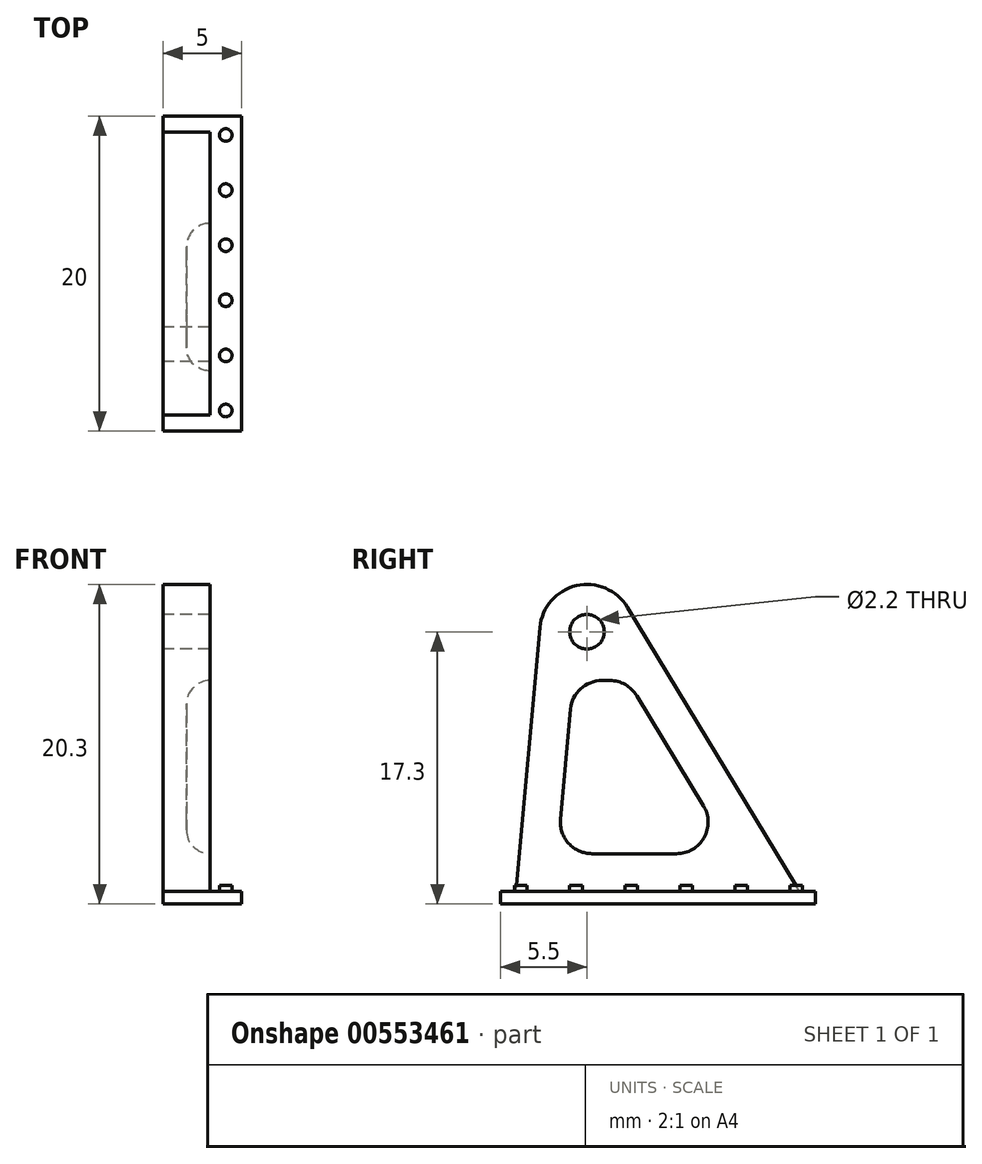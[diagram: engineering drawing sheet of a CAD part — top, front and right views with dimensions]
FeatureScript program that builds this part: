
annotation { "Feature Type Name" : "Feature", "Feature Type Description" : "" }
export const myFeature = defineFeature(function(context is Context, id is Id, definition is map)
    precondition{}
    {
        {
            var Q0;
            Q0=qCreatedBy(makeId("Right.planeOp"),FACE);
            var sketch = newSketch(context, id + "F0", { "sketchPlane" : qUnion([Q0])});
            skLineSegment(sketch, "E0.bottom", {"start": v(-5.5, 0) * mm, "end": v(14.5, 0) * mm});
            skLineSegment(sketch, "E0.top", {"start": v(-5.5, 0.8) * mm, "end": v(14.5, 0.8) * mm});
            skLineSegment(sketch, "E0.left", {"start": v(-5.5, 0) * mm, "end": v(-5.5, 0.8) * mm});
            skLineSegment(sketch, "E0.right", {"start": v(14.5, 0) * mm, "end": v(14.5, 0.8) * mm});
            skSolve(sketch);
        }
        {
            var Q0;
            Q0 = qSketchRegion(id + "F0", true);
            extrude(context, id + "F1", {"entities" : qUnion([Q0]), "depth" : 5 * mm, "offsetDistance" : 25 * mm});
        }
        {
            var Q0;
            Q0=qCreatedBy(makeId("Right.planeOp"),FACE);
            var sketch = newSketch(context, id + "F2", { "sketchPlane" : qUnion([Q0])});
            skCircle(sketch, "E1", {"center": v(0, 17.3) * mm, "radius": 1.1 * mm});
            skLineSegment(sketch, "E2.0", {"start": v(-5.5, 0.8) * mm, "end": v(14.5, 0.8) * mm, "construction": true});
            skLineSegment(sketch, "E3", {"start": v(13.5, 0.8) * mm, "end": v(2.57, 18.85) * mm});
            skLineSegment(sketch, "E4", {"start": v(13.5, 0.8) * mm, "end": v(-4.5, 0.8) * mm});
            skLineSegment(sketch, "E5", {"start": v(-4.5, 0.8) * mm, "end": v(-2.99, 17.57) * mm});
            skArc(sketch, "E6", {"start": v(2.57, 18.85) * mm, "mid": v(-0.68, 20.22) * mm, "end": v(-2.99, 17.57) * mm});
            skSolve(sketch);
        }
        {
            var Q0;
            Q0 = qSketchRegion(id + "F2", true);
            extrude(context, id + "F3", {"entities" : qUnion([Q0]), "operationType" : NewBodyOperationType.ADD, "depth" : 3 * mm, "offsetDistance" : 25 * mm});
        }
        {
            var Q0;
            Q0=makeQuery(id+"F3.opExtrude","CAP_FACE",FACE,{"disambiguationData":[OSD([sQuery(id+"F2.wireOp",EDGE,"E1"),sQuery(id+"F2.wireOp",EDGE,"E3"),sQuery(id+"F2.wireOp",EDGE,"E4"),sQuery(id+"F2.wireOp",EDGE,"E5"),sQuery(id+"F2.wireOp",EDGE,"E6")])],"isStart":false});
            var sketch = newSketch(context, id + "F4", { "sketchPlane" : qUnion([Q0])});
            skLineSegment(sketch, "E7", {"start": v(-1.87, 3.2) * mm, "end": v(9.24, 3.2) * mm});
            skLineSegment(sketch, "E8", {"start": v(9.24, 3.2) * mm, "end": v(2.58, 14.2) * mm});
            skLineSegment(sketch, "E9", {"start": v(2.58, 14.2) * mm, "end": v(-0.88, 14.2) * mm});
            skLineSegment(sketch, "E10", {"start": v(-0.88, 14.2) * mm, "end": v(-1.87, 3.2) * mm});
            skSolve(sketch);
        }
        {
            var Q0;
            Q0 = qSketchRegion(id + "F4", true);
            extrude(context, id + "F5", {"entities" : qUnion([Q0]), "operationType" : NewBodyOperationType.REMOVE, "oppositeDirection" : true, "depth" : 1.5 * mm, "offsetDistance" : 25 * mm});
        }
        {
            var Q0;
            Q0=makeQuery(id+"F5.boolean.opBoolean","COPY",EDGE,{"derivedFrom":makeQuery(id+"F5.opExtrude","SWEPT_EDGE",EDGE,{"disambiguationData":[OSD([sQuery(id+"F4.wireOp",EDGE,"E9"),sQuery(id+"F4.wireOp",EDGE,"E10")])]})});
            var Q1;
            Q1=makeQuery(id+"F5.boolean.opBoolean","COPY",EDGE,{"derivedFrom":makeQuery(id+"F5.opExtrude","SWEPT_EDGE",EDGE,{"disambiguationData":[OSD([sQuery(id+"F4.wireOp",EDGE,"E8"),sQuery(id+"F4.wireOp",EDGE,"E9")])]})});
            var Q2;
            Q2=makeQuery(id+"F5.boolean.opBoolean","COPY",EDGE,{"derivedFrom":makeQuery(id+"F5.opExtrude","SWEPT_EDGE",EDGE,{"disambiguationData":[OSD([sQuery(id+"F4.wireOp",EDGE,"E7"),sQuery(id+"F4.wireOp",EDGE,"E8")])]})});
            var Q3;
            Q3=makeQuery(id+"F5.boolean.opBoolean","COPY",EDGE,{"derivedFrom":makeQuery(id+"F5.opExtrude","SWEPT_EDGE",EDGE,{"disambiguationData":[OSD([sQuery(id+"F4.wireOp",EDGE,"E7"),sQuery(id+"F4.wireOp",EDGE,"E10")])]})});
            fillet(context, id + "F6", {"entities" : qUnion([Q0, Q1, Q2, Q3]), "radius" : 2 * mm, "tangentPropagation" : true, "allowEdgeOverflow" : false});
        }
        {
            var Q0;
            Q0=makeQuery(id+"F5.boolean.opBoolean","COPY",FACE,{"derivedFrom":makeQuery(id+"F5.opExtrude","CAP_FACE",FACE,{"disambiguationData":[OSD([sQuery(id+"F4.wireOp",EDGE,"E7"),sQuery(id+"F4.wireOp",EDGE,"E8"),sQuery(id+"F4.wireOp",EDGE,"E9"),sQuery(id+"F4.wireOp",EDGE,"E10")])],"isStart":false})});
            fillet(context, id + "F7", {"entities" : qUnion([Q0]), "radius" : 1.5 * mm, "tangentPropagation" : true, "allowEdgeOverflow" : false});
        }
        {
            var Q0;
            Q0=makeQuery(id+"F1.opExtrude","SWEPT_FACE",FACE,{"disambiguationData":[OSD([sQuery(id+"F0.wireOp",EDGE,"E0.top")])]});
            var sketch = newSketch(context, id + "F8", { "sketchPlane" : qUnion([Q0])});
            skLineSegment(sketch, "E11", {"start": v(4, 15.15) * mm, "end": v(4, -5.66) * mm, "construction": true});
            skCircle(sketch, "E12", {"center": v(4, 13.3) * mm, "radius": 0.4 * mm});
            skCircle(sketch, "E13.1.0.0", {"center": v(4, 9.8) * mm, "radius": 0.4 * mm});
            skCircle(sketch, "E13.2.0.0", {"center": v(4, 6.3) * mm, "radius": 0.4 * mm});
            skCircle(sketch, "E13.3.0.0", {"center": v(4, 2.8) * mm, "radius": 0.4 * mm});
            skCircle(sketch, "E13.4.0.0", {"center": v(4, -0.7) * mm, "radius": 0.4 * mm});
            skCircle(sketch, "E13.5.0.0", {"center": v(4, -4.2) * mm, "radius": 0.4 * mm});
            skLineSegment(sketch, "E13.direction1", {"start": v(4, 13.3) * mm, "end": v(4, 9.8) * mm, "construction": true});
            skSolve(sketch);
        }
        {
            var Q0;
            Q0 = qSketchRegion(id + "F8", true);
            extrude(context, id + "F9", {"entities" : qUnion([Q0]), "operationType" : NewBodyOperationType.ADD, "depth" : 0.4 * mm, "offsetDistance" : 25 * mm});
        }
    });
